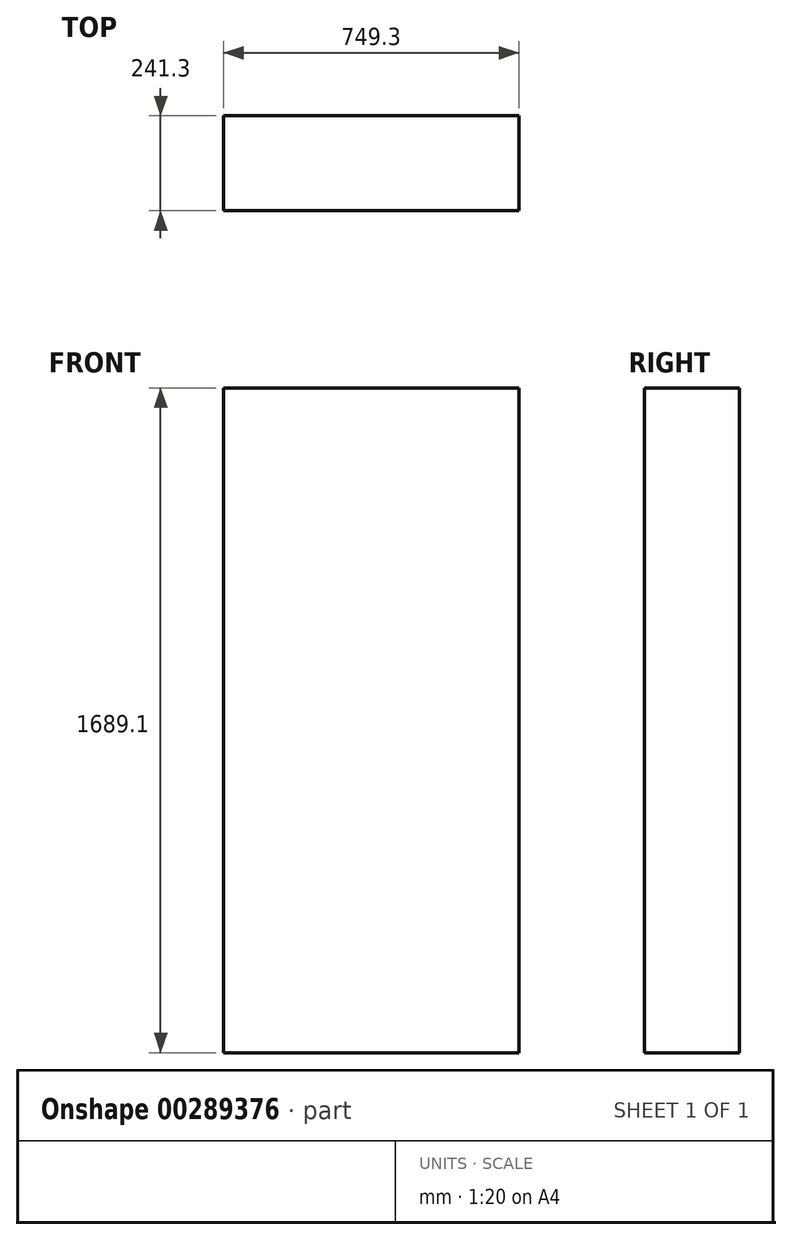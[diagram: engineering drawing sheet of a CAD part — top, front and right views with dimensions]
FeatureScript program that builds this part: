
annotation { "Feature Type Name" : "Feature", "Feature Type Description" : "" }
export const myFeature = defineFeature(function(context is Context, id is Id, definition is map)
    precondition{}
    {
        {
            var Q0;
            Q0=qCreatedBy(makeId("Front.planeOp"),FACE);
            var sketch = newSketch(context, id + "F0", { "sketchPlane" : qUnion([Q0])});
            skLineSegment(sketch, "E0.bottom", {"start": v(374.65, 844.55) * mm, "end": v(-374.65, 844.55) * mm});
            skLineSegment(sketch, "E0.top", {"start": v(374.65, -844.55) * mm, "end": v(-374.65, -844.55) * mm});
            skLineSegment(sketch, "E0.left", {"start": v(374.65, 844.55) * mm, "end": v(374.65, -844.55) * mm});
            skLineSegment(sketch, "E0.right", {"start": v(-374.65, 844.55) * mm, "end": v(-374.65, -844.55) * mm});
            skPoint(sketch, "E0.middle", {"position": v(0, 0) * mm});
            skSolve(sketch);
        }
        {
            var Q0;
            Q0=makeQuery(id+"F0.imprint","IMPRINT",FACE,{"disambiguationData":[TD([[makeQuery(id+"F0.imprint","IMPRINT",EDGE,{"derivedFrom":sQuery(id+"F0.wireOp",EDGE,"E0.bottom")}),1.0]])]});
            extrude(context, id + "F1", {"entities" : qUnion([Q0]), "depth" : 241.3 * mm});
        }
    });
